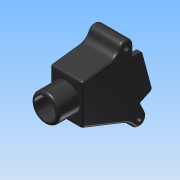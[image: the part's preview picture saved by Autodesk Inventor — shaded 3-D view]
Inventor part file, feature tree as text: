
AUTODESK INVENTOR PART (.ipt)
format: ipt  version: 2014 (Build 180170000, 170)  size: 252,416 bytes
history: native  units: in
note: dims shown in document units (in); Inventor stores cm internally (conversion verified against a paired STEP export)
features: extrude x4, sketch x4, fillet x1, projected_geometry x1
ambient origin geometry x8: Origin, YZ Plane, XZ Plane, XY Plane, X Axis, Y Axis, Z Axis, Center Point
bodies: Solid1 (feature_tree)
feature tree (10):
  extrude  "Extrusion1"  Depth=0.34in
  extrude  "Extrusion2"  Depth=0.3in
  extrude  "Extrusion3"  Depth=0.5603in
  extrude  "Extrusion4"  Depth=0.0625in
  fillet  "Fillet1"  Radius=0.43in
  sketch  "Sketch1"  dims[d0=0.116in d1=0.34in]
  sketch  "Sketch2"  dims[d2=0.95in d3=0.3in]
  sketch  "Sketch4"  dims[d4=0.475in d5=0.5603in]
  projected_geometry  "Projected Loop1"
  sketch  "Sketch5"  dims[d6=1.652in d7=1.3in d8=0.43in d9=0.958in d10=1.425in d11=1.67in d12=1.69in d15=0.79in d16=0.0in d17=15.0deg d20=0.5in d21=0.25in d22=0.663in d23=0.51in d24=0.51in d25=0.0in d26=0.1in d27=0.58in d28=0.0in d29=0.58in d30=0.0in d31=0.0625in]
